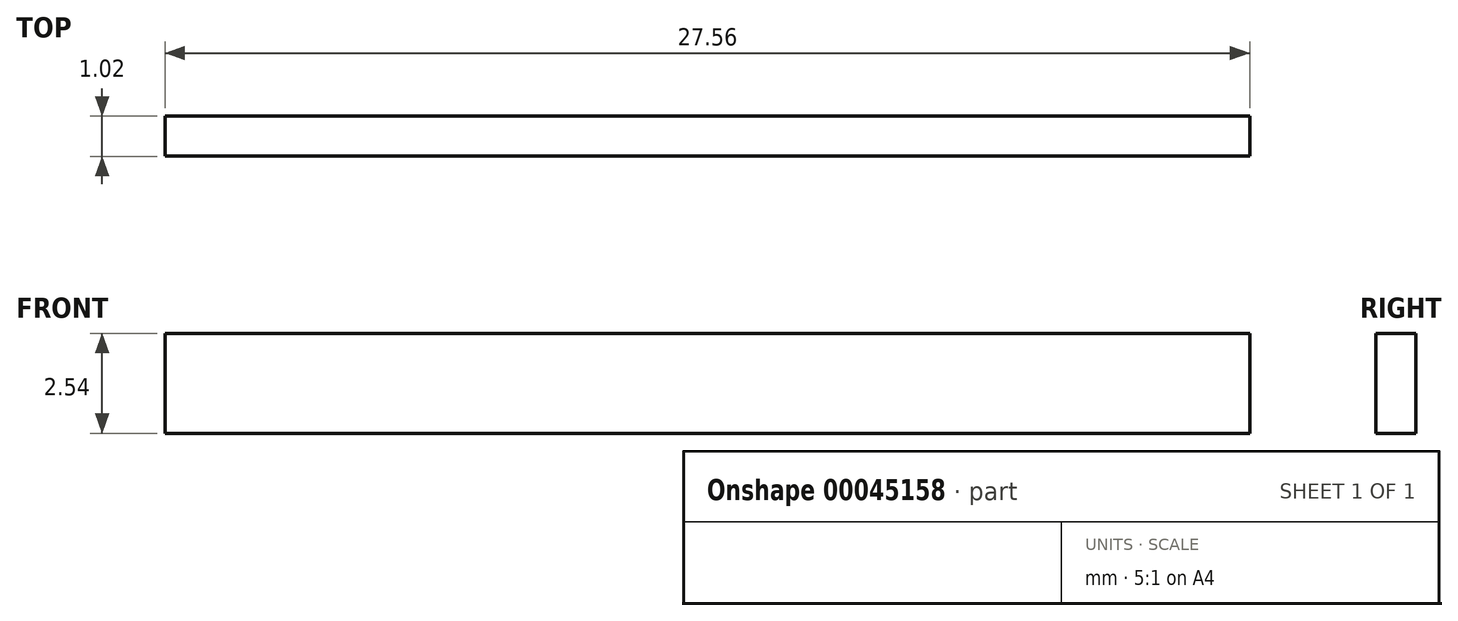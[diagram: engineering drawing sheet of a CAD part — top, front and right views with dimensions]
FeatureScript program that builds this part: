
annotation { "Feature Type Name" : "Feature", "Feature Type Description" : "" }
export const myFeature = defineFeature(function(context is Context, id is Id, definition is map)
    precondition{}
    {
        {
            var Q0;
            Q0=qCreatedBy(makeId("Front.planeOp"),FACE);
            var sketch = newSketch(context, id + "F0", { "sketchPlane" : qUnion([Q0])});
            skLineSegment(sketch, "E0", {"start": v(-12.38, 1.39) * mm, "end": v(15.18, 1.39) * mm});
            skLineSegment(sketch, "E1", {"start": v(-12.38, -1.15) * mm, "end": v(-12.38, 1.39) * mm});
            skLineSegment(sketch, "E2", {"start": v(-12.38, -1.15) * mm, "end": v(15.18, -1.15) * mm});
            skLineSegment(sketch, "E3", {"start": v(15.18, -1.15) * mm, "end": v(15.18, 1.39) * mm});
            skSolve(sketch);
        }
        {
            var Q0;
            Q0 = qSketchRegion(id + "F0", true);
            extrude(context, id + "F1", {"entities" : qUnion([Q0]), "depth" : 1.02 * mm});
        }
    });
